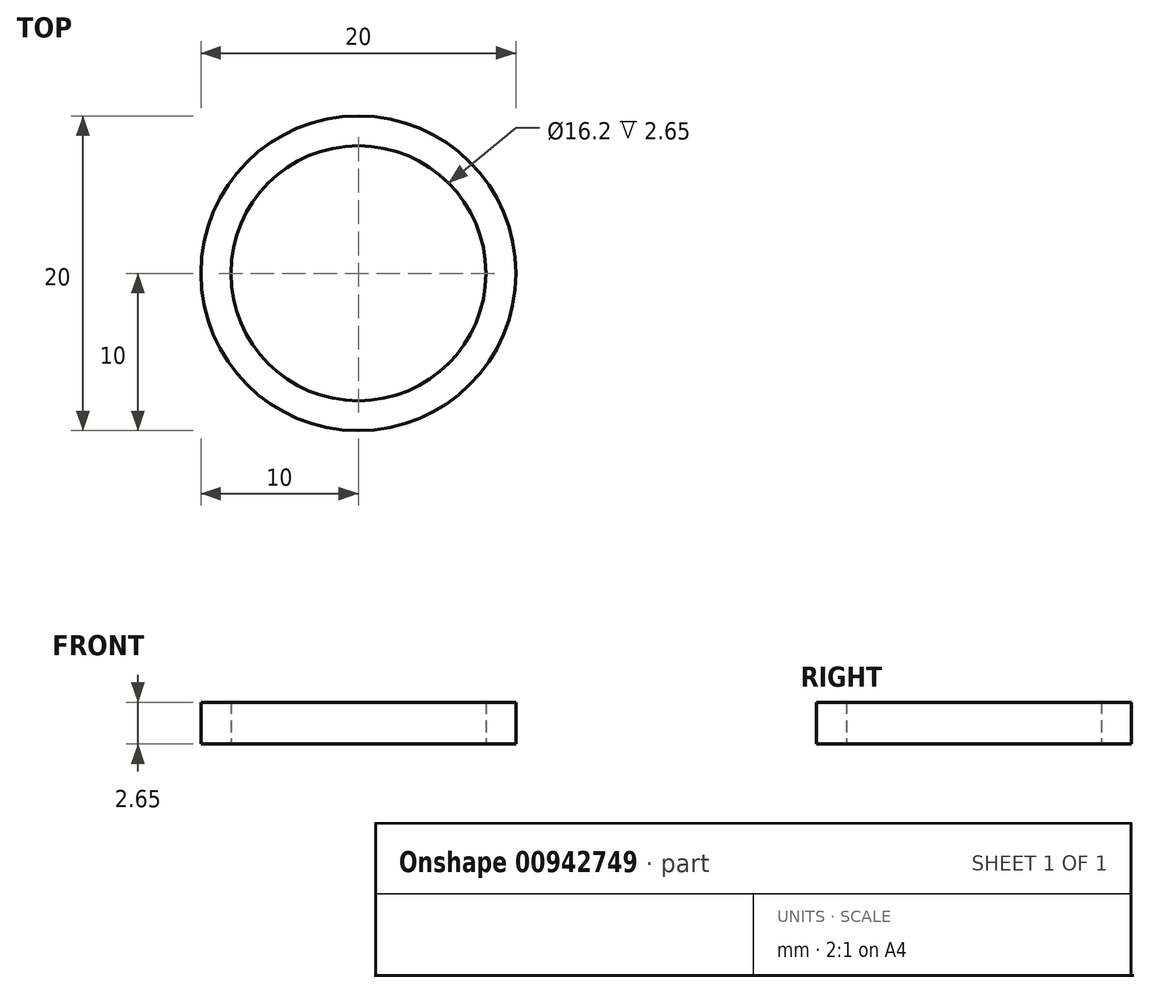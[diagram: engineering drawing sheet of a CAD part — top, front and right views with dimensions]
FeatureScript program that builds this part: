
annotation { "Feature Type Name" : "Feature", "Feature Type Description" : "" }
export const myFeature = defineFeature(function(context is Context, id is Id, definition is map)
    precondition{}
    {
        {
            var Q0;
            Q0=qCreatedBy(makeId("Top.planeOp"),FACE);
            var sketch = newSketch(context, id + "F0", { "sketchPlane" : qUnion([Q0])});
            skCircle(sketch, "E0", {"center": v(0, 0) * mm, "radius": 8.1 * mm});
            skCircle(sketch, "E1", {"center": v(0, 0) * mm, "radius": 10 * mm});
            skSolve(sketch);
        }
        {
            var Q0;
            Q0=makeQuery(id+"F0.imprint","IMPRINT",FACE,{"disambiguationData":[TD([[makeQuery(id+"F0.imprint","IMPRINT",EDGE,{"derivedFrom":sQuery(id+"F0.wireOp",EDGE,"E0")}),-1.0]])]});
            extrude(context, id + "F1", {"entities" : qUnion([Q0]), "depth" : 2.65 * mm, "offsetDistance" : 25 * mm});
        }
    });
